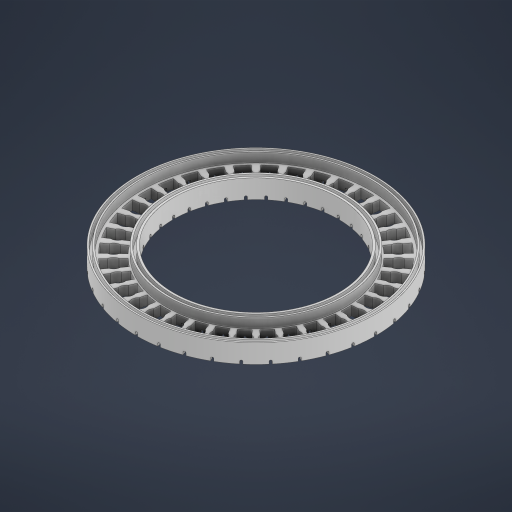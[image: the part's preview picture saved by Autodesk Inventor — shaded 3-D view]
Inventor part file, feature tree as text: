
AUTODESK INVENTOR PART (.ipt)
format: ipt  version: 2024 (Build 280153000, 153)  size: 1,221,632 bytes
history: native  units: mm
features: extrude x4, sketch x4, fillet x1, pattern_circular x1, projected_geometry x1
ambient origin geometry x8: Origin, YZ Plane, XZ Plane, XY Plane, X Axis, Y Axis, Z Axis, Center Point
bodies: Solid1 (feature_tree)
feature tree (11):
  extrude  "Extrusion1"  Depth=8.0mm TaperAngle=0.0deg
  extrude  "Extrusion2"  Depth=8.0mm TaperAngle=0.0deg
  extrude  "Extrusion3"  Depth=360.0mm TaperAngle=360.0deg
  extrude  "Extrusion4"  Depth=1.0mm
  fillet  "Fillet1"  Radius=360.0mm
  pattern_circular  "Circular Pattern1"  [2 undecoded]
  sketch  "Sketch1"  dims[d0=8.0mm d1=0.0mm d2=8.0mm d3=0.0mm]
  sketch  "Sketch2"  dims[d5=360.0mm d6=145.0mm d7=200.0mm d8=360.0deg d9=8.0mm d10=0.0mm]
  sketch  "Sketch3"  dims[d11=12.0mm d12=360.0mm d14=360.0deg]
  projected_geometry  "Projected Loop1"
  sketch  "Sketch5"  dims[d16=3.0mm d17=0.0mm d18=1.0mm d19=360.0mm d20=360.0deg]
note: 2 required parameter values undecoded (feature->parameter linkage not recoverable at this tier; creation-order binding heuristic only, values carry confidence <= 0.55)
